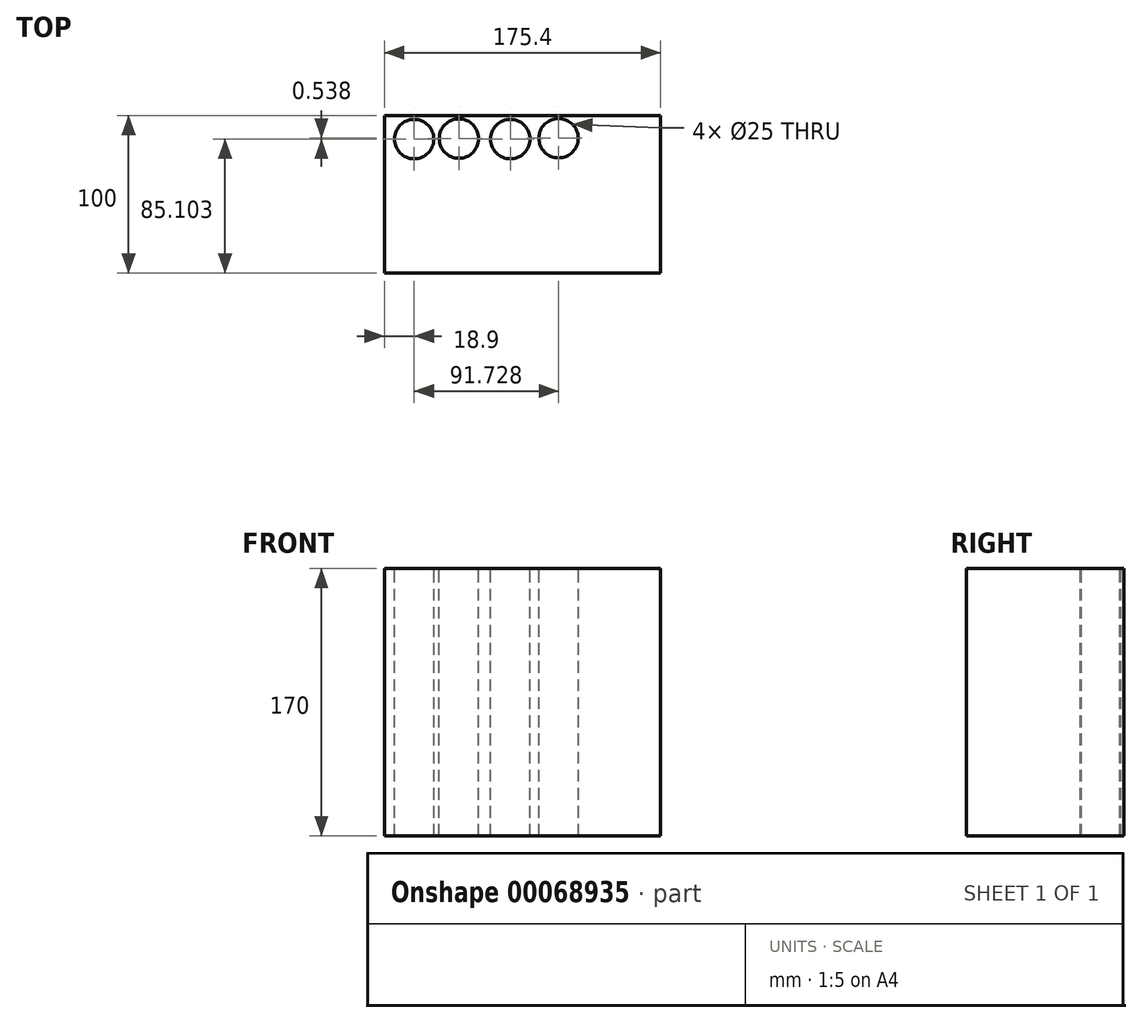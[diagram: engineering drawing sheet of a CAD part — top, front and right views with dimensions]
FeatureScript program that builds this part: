
annotation { "Feature Type Name" : "Feature", "Feature Type Description" : "" }
export const myFeature = defineFeature(function(context is Context, id is Id, definition is map)
    precondition{}
    {
        {
            var Q0;
            Q0=qCreatedBy(makeId("Top.planeOp"),FACE);
            var sketch = newSketch(context, id + "F0", { "sketchPlane" : qUnion([Q0])});
            skLineSegment(sketch, "E0.bottom", {"start": v(-83.56, 50.1) * mm, "end": v(91.84, 50.1) * mm});
            skLineSegment(sketch, "E0.top", {"start": v(-83.56, -49.9) * mm, "end": v(91.84, -49.9) * mm});
            skLineSegment(sketch, "E0.left", {"start": v(-83.56, 50.1) * mm, "end": v(-83.56, -49.9) * mm});
            skLineSegment(sketch, "E0.right", {"start": v(91.84, 50.1) * mm, "end": v(91.84, -49.9) * mm});
            skSolve(sketch);
        }
        {
            var Q0;
            Q0=makeQuery(id+"F0.imprint","IMPRINT",FACE,{"disambiguationData":[TD([[makeQuery(id+"F0.imprint","IMPRINT",EDGE,{"derivedFrom":sQuery(id+"F0.wireOp",EDGE,"E0.bottom")}),-1.0]])]});
            extrude(context, id + "F1", {"entities" : qUnion([Q0]), "depth" : 170 * mm});
        }
        {
            var Q0;
            Q0=makeQuery(id+"F1.opExtrude","CAP_FACE",FACE,{"disambiguationData":[OSD([sQuery(id+"F0.wireOp",EDGE,"E0.bottom"),sQuery(id+"F0.wireOp",EDGE,"E0.top"),sQuery(id+"F0.wireOp",EDGE,"E0.left"),sQuery(id+"F0.wireOp",EDGE,"E0.right")])],"isStart":false});
            var sketch = newSketch(context, id + "F2", { "sketchPlane" : qUnion([Q0])});
            skCircle(sketch, "E1", {"center": v(-64.66, 35.2) * mm, "radius": 12.55 * mm});
            skCircle(sketch, "E2", {"center": v(-36.22, 35.51) * mm, "radius": 12.55 * mm});
            skCircle(sketch, "E3", {"center": v(-3.6, 35.2) * mm, "radius": 12.55 * mm});
            skCircle(sketch, "E4", {"center": v(27.07, 35.74) * mm, "radius": 12.55 * mm});
            skSolve(sketch);
        }
        {
            var Q0;
            Q0=sQuery(id+"F2.wireOp",VERTEX,"E4.center");
            var Q1;
            Q1=sQuery(id+"F2.wireOp",VERTEX,"E3.center");
            var Q2;
            Q2=sQuery(id+"F2.wireOp",VERTEX,"E2.center");
            var Q3;
            Q3=sQuery(id+"F2.wireOp",VERTEX,"E1.center");
            var Q4;
            Q4=makeQuery(id+"F1.opExtrude","SWEPT_BODY",BODY,{"disambiguationData":[OSD([sQuery(id+"F0.wireOp",EDGE,"E0.bottom"),sQuery(id+"F0.wireOp",EDGE,"E0.top"),sQuery(id+"F0.wireOp",EDGE,"E0.left"),sQuery(id+"F0.wireOp",EDGE,"E0.right")])]});
            hole(context, id + "F3", {"style" : HoleStyle.SIMPLE, "holeDiameter" : 25 * mm, "endStyle" : HoleEndStyle.THROUGH, "locations" : qUnion([Q0, Q1, Q2, Q3]), "scope" : qUnion([Q4])});
        }
    });
